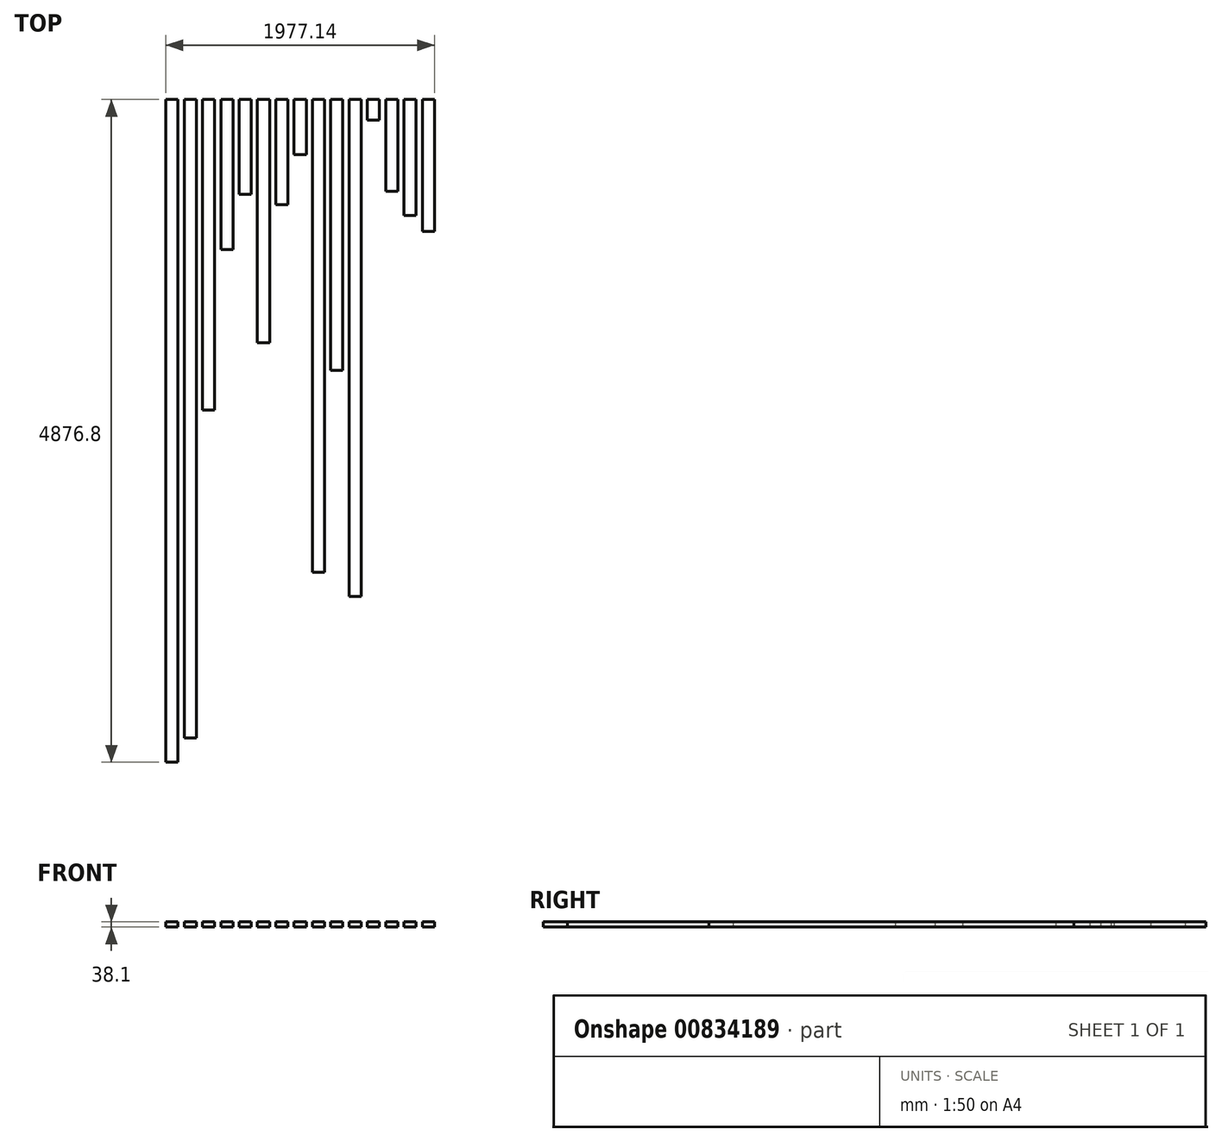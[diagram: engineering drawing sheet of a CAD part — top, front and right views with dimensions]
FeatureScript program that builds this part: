
annotation { "Feature Type Name" : "Feature", "Feature Type Description" : "" }
export const myFeature = defineFeature(function(context is Context, id is Id, definition is map)
    precondition{}
    {
        {
            var Q0;
            Q0=qCreatedBy(makeId("Front.planeOp"),FACE);
            var sketch = newSketch(context, id + "F0", { "sketchPlane" : qUnion([Q0])});
            skLineSegment(sketch, "E0.bottom", {"start": v(44.45, 19.05) * mm, "end": v(-44.45, 19.05) * mm});
            skLineSegment(sketch, "E0.top", {"start": v(44.45, -19.05) * mm, "end": v(-44.45, -19.05) * mm});
            skLineSegment(sketch, "E0.left", {"start": v(44.45, 19.05) * mm, "end": v(44.45, -19.05) * mm});
            skLineSegment(sketch, "E0.right", {"start": v(-44.45, 19.05) * mm, "end": v(-44.45, -19.05) * mm});
            skPoint(sketch, "E0.middle", {"position": v(0, 0) * mm});
            skLineSegment(sketch, "E1.1.0.0", {"start": v(90.42, 19.05) * mm, "end": v(90.42, -19.05) * mm});
            skLineSegment(sketch, "E1.1.0.1", {"start": v(179.32, 19.05) * mm, "end": v(90.42, 19.05) * mm});
            skLineSegment(sketch, "E1.1.0.2", {"start": v(179.32, -19.05) * mm, "end": v(90.42, -19.05) * mm});
            skLineSegment(sketch, "E1.1.0.3", {"start": v(179.32, 19.05) * mm, "end": v(179.32, -19.05) * mm});
            skLineSegment(sketch, "E1.2.0.0", {"start": v(225.3, 19.05) * mm, "end": v(225.3, -19.05) * mm});
            skLineSegment(sketch, "E1.2.0.1", {"start": v(314.2, 19.05) * mm, "end": v(225.3, 19.05) * mm});
            skLineSegment(sketch, "E1.2.0.2", {"start": v(314.2, -19.05) * mm, "end": v(225.3, -19.05) * mm});
            skLineSegment(sketch, "E1.2.0.3", {"start": v(314.2, 19.05) * mm, "end": v(314.2, -19.05) * mm});
            skLineSegment(sketch, "E1.3.0.0", {"start": v(360.17, 19.05) * mm, "end": v(360.17, -19.05) * mm});
            skLineSegment(sketch, "E1.3.0.1", {"start": v(449.07, 19.05) * mm, "end": v(360.17, 19.05) * mm});
            skLineSegment(sketch, "E1.3.0.2", {"start": v(449.07, -19.05) * mm, "end": v(360.17, -19.05) * mm});
            skLineSegment(sketch, "E1.3.0.3", {"start": v(449.07, 19.05) * mm, "end": v(449.07, -19.05) * mm});
            skLineSegment(sketch, "E1.4.0.0", {"start": v(495.05, 19.05) * mm, "end": v(495.05, -19.05) * mm});
            skLineSegment(sketch, "E1.4.0.1", {"start": v(583.95, 19.05) * mm, "end": v(495.05, 19.05) * mm});
            skLineSegment(sketch, "E1.4.0.2", {"start": v(583.95, -19.05) * mm, "end": v(495.05, -19.05) * mm});
            skLineSegment(sketch, "E1.4.0.3", {"start": v(583.95, 19.05) * mm, "end": v(583.95, -19.05) * mm});
            skLineSegment(sketch, "E1.5.0.0", {"start": v(629.92, 19.05) * mm, "end": v(629.92, -19.05) * mm});
            skLineSegment(sketch, "E1.5.0.1", {"start": v(718.82, 19.05) * mm, "end": v(629.92, 19.05) * mm});
            skLineSegment(sketch, "E1.5.0.2", {"start": v(718.82, -19.05) * mm, "end": v(629.92, -19.05) * mm});
            skLineSegment(sketch, "E1.5.0.3", {"start": v(718.82, 19.05) * mm, "end": v(718.82, -19.05) * mm});
            skLineSegment(sketch, "E1.direction1", {"start": v(-44.45, -19.05) * mm, "end": v(90.42, -19.05) * mm, "construction": true});
            skLineSegment(sketch, "E2.0.6.0", {"start": v(764.8, 19.05) * mm, "end": v(764.8, -19.05) * mm});
            skLineSegment(sketch, "E2.3.6.0", {"start": v(853.7, 19.05) * mm, "end": v(764.8, 19.05) * mm});
            skLineSegment(sketch, "E2.6.6.0", {"start": v(853.7, -19.05) * mm, "end": v(764.8, -19.05) * mm});
            skLineSegment(sketch, "E2.9.6.0", {"start": v(853.7, 19.05) * mm, "end": v(853.7, -19.05) * mm});
            skLineSegment(sketch, "E2.0.7.0", {"start": v(899.67, 19.05) * mm, "end": v(899.67, -19.05) * mm});
            skLineSegment(sketch, "E2.3.7.0", {"start": v(988.57, 19.05) * mm, "end": v(899.67, 19.05) * mm});
            skLineSegment(sketch, "E2.6.7.0", {"start": v(988.57, -19.05) * mm, "end": v(899.67, -19.05) * mm});
            skLineSegment(sketch, "E2.9.7.0", {"start": v(988.57, 19.05) * mm, "end": v(988.57, -19.05) * mm});
            skLineSegment(sketch, "E2.0.8.0", {"start": v(1034.54, 19.05) * mm, "end": v(1034.54, -19.05) * mm});
            skLineSegment(sketch, "E2.3.8.0", {"start": v(1123.44, 19.05) * mm, "end": v(1034.54, 19.05) * mm});
            skLineSegment(sketch, "E2.6.8.0", {"start": v(1123.44, -19.05) * mm, "end": v(1034.54, -19.05) * mm});
            skLineSegment(sketch, "E2.9.8.0", {"start": v(1123.44, 19.05) * mm, "end": v(1123.44, -19.05) * mm});
            skLineSegment(sketch, "E2.0.9.0", {"start": v(1169.42, 19.05) * mm, "end": v(1169.42, -19.05) * mm});
            skLineSegment(sketch, "E2.3.9.0", {"start": v(1258.32, 19.05) * mm, "end": v(1169.42, 19.05) * mm});
            skLineSegment(sketch, "E2.6.9.0", {"start": v(1258.32, -19.05) * mm, "end": v(1169.42, -19.05) * mm});
            skLineSegment(sketch, "E2.9.9.0", {"start": v(1258.32, 19.05) * mm, "end": v(1258.32, -19.05) * mm});
            skLineSegment(sketch, "E3.0.10.0", {"start": v(1304.29, 19.05) * mm, "end": v(1304.29, -19.05) * mm});
            skLineSegment(sketch, "E3.3.10.0", {"start": v(1393.19, 19.05) * mm, "end": v(1304.29, 19.05) * mm});
            skLineSegment(sketch, "E3.6.10.0", {"start": v(1393.19, -19.05) * mm, "end": v(1304.29, -19.05) * mm});
            skLineSegment(sketch, "E3.9.10.0", {"start": v(1393.19, 19.05) * mm, "end": v(1393.19, -19.05) * mm});
            skLineSegment(sketch, "E3.0.11.0", {"start": v(1439.16, 19.05) * mm, "end": v(1439.16, -19.05) * mm});
            skLineSegment(sketch, "E3.3.11.0", {"start": v(1528.06, 19.05) * mm, "end": v(1439.16, 19.05) * mm});
            skLineSegment(sketch, "E3.6.11.0", {"start": v(1528.06, -19.05) * mm, "end": v(1439.16, -19.05) * mm});
            skLineSegment(sketch, "E3.9.11.0", {"start": v(1528.06, 19.05) * mm, "end": v(1528.06, -19.05) * mm});
            skLineSegment(sketch, "E3.0.12.0", {"start": v(1574.04, 19.05) * mm, "end": v(1574.04, -19.05) * mm});
            skLineSegment(sketch, "E3.3.12.0", {"start": v(1662.94, 19.05) * mm, "end": v(1574.04, 19.05) * mm});
            skLineSegment(sketch, "E3.6.12.0", {"start": v(1662.94, -19.05) * mm, "end": v(1574.04, -19.05) * mm});
            skLineSegment(sketch, "E3.9.12.0", {"start": v(1662.94, 19.05) * mm, "end": v(1662.94, -19.05) * mm});
            skLineSegment(sketch, "E3.0.13.0", {"start": v(1708.91, 19.05) * mm, "end": v(1708.91, -19.05) * mm});
            skLineSegment(sketch, "E3.3.13.0", {"start": v(1797.81, 19.05) * mm, "end": v(1708.91, 19.05) * mm});
            skLineSegment(sketch, "E3.6.13.0", {"start": v(1797.81, -19.05) * mm, "end": v(1708.91, -19.05) * mm});
            skLineSegment(sketch, "E3.9.13.0", {"start": v(1797.81, 19.05) * mm, "end": v(1797.81, -19.05) * mm});
            skLineSegment(sketch, "E3.0.14.0", {"start": v(1843.79, 19.05) * mm, "end": v(1843.79, -19.05) * mm});
            skLineSegment(sketch, "E3.3.14.0", {"start": v(1932.69, 19.05) * mm, "end": v(1843.79, 19.05) * mm});
            skLineSegment(sketch, "E3.6.14.0", {"start": v(1932.69, -19.05) * mm, "end": v(1843.79, -19.05) * mm});
            skLineSegment(sketch, "E3.9.14.0", {"start": v(1932.69, 19.05) * mm, "end": v(1932.69, -19.05) * mm});
            skSolve(sketch);
        }
        {
            var Q0;
            Q0=makeQuery(id+"F0.imprint","IMPRINT",FACE,{"disambiguationData":[TD([[makeQuery(id+"F0.imprint","IMPRINT",EDGE,{"derivedFrom":sQuery(id+"F0.wireOp",EDGE,"E0.bottom")}),1.0]])]});
            extrude(context, id + "F1", {"entities" : qUnion([Q0]), "depth" : 4876.8 * mm, "offsetDistance" : 25.4 * mm});
        }
        {
            var Q0;
            Q0=makeQuery(id+"F0.imprint","IMPRINT",FACE,{"disambiguationData":[TD([[makeQuery(id+"F0.imprint","IMPRINT",EDGE,{"derivedFrom":sQuery(id+"F0.wireOp",EDGE,"E1.1.0.0")}),1.0]])]});
            extrude(context, id + "F2", {"entities" : qUnion([Q0]), "depth" : 4699 * mm, "offsetDistance" : 25.4 * mm});
        }
        {
            var Q0;
            Q0=makeQuery(id+"F0.imprint","IMPRINT",FACE,{"disambiguationData":[TD([[makeQuery(id+"F0.imprint","IMPRINT",EDGE,{"derivedFrom":sQuery(id+"F0.wireOp",EDGE,"E1.2.0.0")}),1.0]])]});
            extrude(context, id + "F3", {"entities" : qUnion([Q0]), "depth" : 2286 * mm, "offsetDistance" : 25.4 * mm});
        }
        {
            var Q0;
            Q0=makeQuery(id+"F0.imprint","IMPRINT",FACE,{"disambiguationData":[TD([[makeQuery(id+"F0.imprint","IMPRINT",EDGE,{"derivedFrom":sQuery(id+"F0.wireOp",EDGE,"E1.3.0.0")}),1.0]])]});
            extrude(context, id + "F4", {"entities" : qUnion([Q0]), "depth" : 1104.9 * mm, "offsetDistance" : 25.4 * mm});
        }
        {
            var Q0;
            Q0=makeQuery(id+"F0.imprint","IMPRINT",FACE,{"disambiguationData":[TD([[makeQuery(id+"F0.imprint","IMPRINT",EDGE,{"derivedFrom":sQuery(id+"F0.wireOp",EDGE,"E1.4.0.0")}),1.0]])]});
            extrude(context, id + "F5", {"entities" : qUnion([Q0]), "depth" : 698.5 * mm, "offsetDistance" : 25.4 * mm});
        }
        {
            var Q0;
            Q0=makeQuery(id+"F0.imprint","IMPRINT",FACE,{"disambiguationData":[TD([[makeQuery(id+"F0.imprint","IMPRINT",EDGE,{"derivedFrom":sQuery(id+"F0.wireOp",EDGE,"E1.5.0.0")}),1.0]])]});
            extrude(context, id + "F6", {"entities" : qUnion([Q0]), "depth" : 1790.7 * mm, "offsetDistance" : 25.4 * mm});
        }
        {
            var Q0;
            Q0=makeQuery(id+"F0.imprint","IMPRINT",FACE,{"disambiguationData":[TD([[makeQuery(id+"F0.imprint","IMPRINT",EDGE,{"derivedFrom":sQuery(id+"F0.wireOp",EDGE,"E2.0.6.0")}),1.0]])]});
            extrude(context, id + "F7", {"entities" : qUnion([Q0]), "depth" : 774.7 * mm, "offsetDistance" : 25.4 * mm});
        }
        {
            var Q0;
            Q0=makeQuery(id+"F0.imprint","IMPRINT",FACE,{"disambiguationData":[TD([[makeQuery(id+"F0.imprint","IMPRINT",EDGE,{"derivedFrom":sQuery(id+"F0.wireOp",EDGE,"E2.0.7.0")}),1.0]])]});
            extrude(context, id + "F8", {"entities" : qUnion([Q0]), "depth" : 406.4 * mm, "offsetDistance" : 25.4 * mm});
        }
        {
            var Q0;
            Q0=makeQuery(id+"F0.imprint","IMPRINT",FACE,{"disambiguationData":[TD([[makeQuery(id+"F0.imprint","IMPRINT",EDGE,{"derivedFrom":sQuery(id+"F0.wireOp",EDGE,"E2.0.8.0")}),1.0]])]});
            extrude(context, id + "F9", {"entities" : qUnion([Q0]), "depth" : 3479.8 * mm, "offsetDistance" : 25.4 * mm});
        }
        {
            var Q0;
            Q0=makeQuery(id+"F0.imprint","IMPRINT",FACE,{"disambiguationData":[TD([[makeQuery(id+"F0.imprint","IMPRINT",EDGE,{"derivedFrom":sQuery(id+"F0.wireOp",EDGE,"E2.0.9.0")}),1.0]])]});
            extrude(context, id + "F10", {"entities" : qUnion([Q0]), "depth" : 1993.9 * mm, "offsetDistance" : 25.4 * mm});
        }
        {
            var Q0;
            Q0=makeQuery(id+"F0.imprint","IMPRINT",FACE,{"disambiguationData":[TD([[makeQuery(id+"F0.imprint","IMPRINT",EDGE,{"derivedFrom":sQuery(id+"F0.wireOp",EDGE,"E3.0.10.0")}),1.0]])]});
            extrude(context, id + "F11", {"entities" : qUnion([Q0]), "depth" : 3657.6 * mm, "offsetDistance" : 25.4 * mm});
        }
        {
            var Q0;
            Q0=makeQuery(id+"F0.imprint","IMPRINT",FACE,{"disambiguationData":[TD([[makeQuery(id+"F0.imprint","IMPRINT",EDGE,{"derivedFrom":sQuery(id+"F0.wireOp",EDGE,"E3.0.11.0")}),1.0]])]});
            extrude(context, id + "F12", {"entities" : qUnion([Q0]), "depth" : 152.4 * mm, "offsetDistance" : 25.4 * mm});
        }
        {
            var Q0;
            Q0=makeQuery(id+"F0.imprint","IMPRINT",FACE,{"disambiguationData":[TD([[makeQuery(id+"F0.imprint","IMPRINT",EDGE,{"derivedFrom":sQuery(id+"F0.wireOp",EDGE,"E3.0.12.0")}),1.0]])]});
            extrude(context, id + "F13", {"entities" : qUnion([Q0]), "depth" : 676.27 * mm, "offsetDistance" : 25.4 * mm});
        }
        {
            var Q0;
            Q0=makeQuery(id+"F0.imprint","IMPRINT",FACE,{"disambiguationData":[TD([[makeQuery(id+"F0.imprint","IMPRINT",EDGE,{"derivedFrom":sQuery(id+"F0.wireOp",EDGE,"E3.0.13.0")}),1.0]])]});
            extrude(context, id + "F14", {"entities" : qUnion([Q0]), "depth" : 854.07 * mm, "offsetDistance" : 25.4 * mm});
        }
        {
            var Q0;
            Q0=makeQuery(id+"F0.imprint","IMPRINT",FACE,{"disambiguationData":[TD([[makeQuery(id+"F0.imprint","IMPRINT",EDGE,{"derivedFrom":sQuery(id+"F0.wireOp",EDGE,"E3.0.14.0")}),1.0]])]});
            extrude(context, id + "F15", {"entities" : qUnion([Q0]), "depth" : 971.55 * mm, "offsetDistance" : 25.4 * mm});
        }
    });
